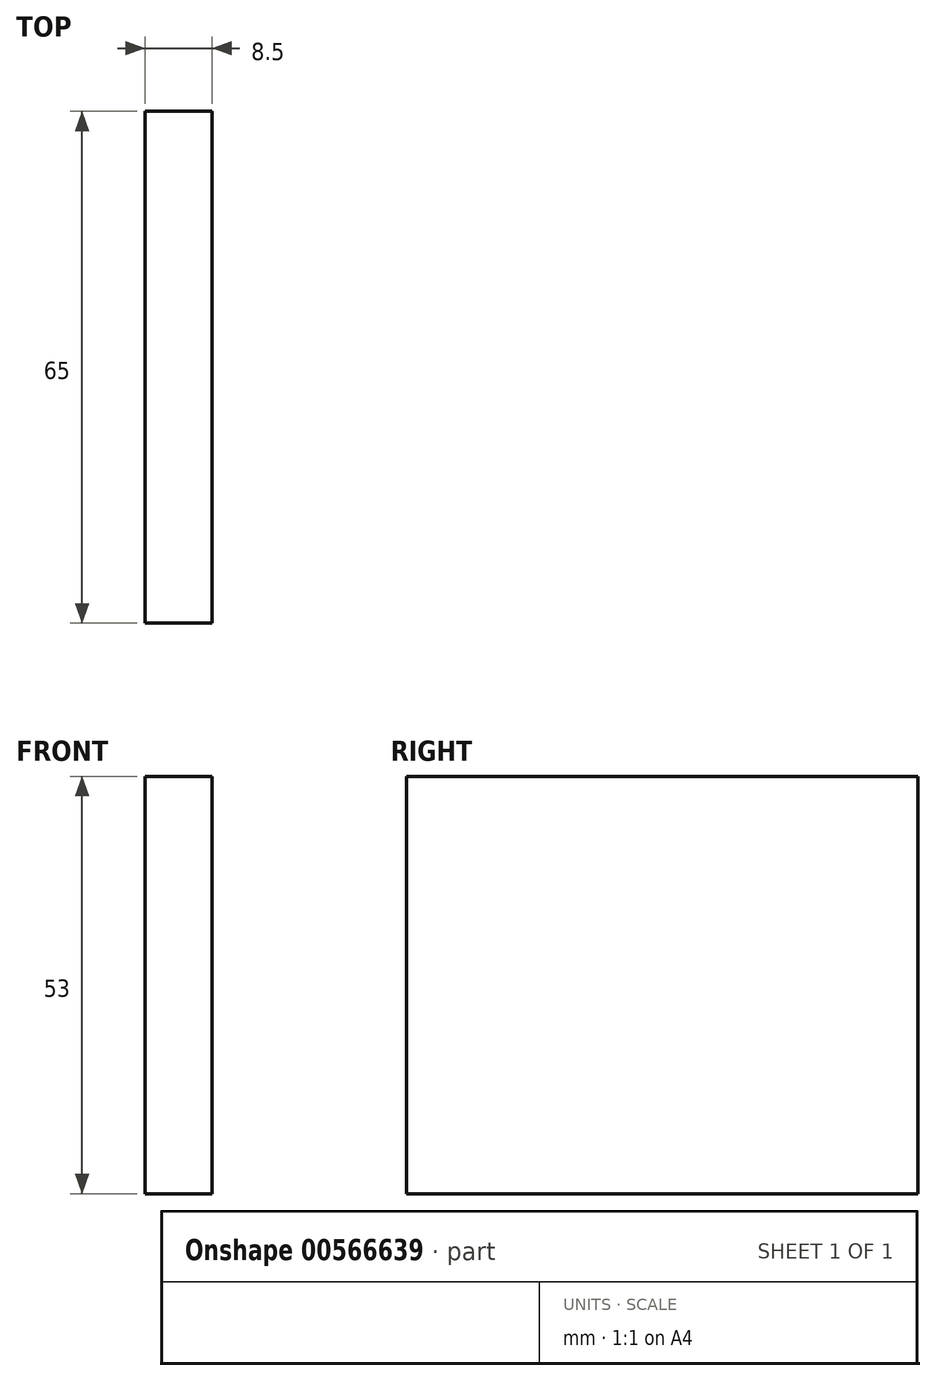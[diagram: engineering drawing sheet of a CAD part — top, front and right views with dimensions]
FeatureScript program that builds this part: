
annotation { "Feature Type Name" : "Feature", "Feature Type Description" : "" }
export const myFeature = defineFeature(function(context is Context, id is Id, definition is map)
    precondition{}
    {
        {
            var Q0;
            Q0=qCreatedBy(makeId("Right.planeOp"),FACE);
            var sketch = newSketch(context, id + "F0", { "sketchPlane" : qUnion([Q0])});
            skLineSegment(sketch, "E0.bottom", {"start": v(-32.5, 26.5) * mm, "end": v(32.5, 26.5) * mm});
            skLineSegment(sketch, "E0.top", {"start": v(-32.5, -26.5) * mm, "end": v(32.5, -26.5) * mm});
            skLineSegment(sketch, "E0.left", {"start": v(-32.5, 26.5) * mm, "end": v(-32.5, -26.5) * mm});
            skLineSegment(sketch, "E0.right", {"start": v(32.5, 26.5) * mm, "end": v(32.5, -26.5) * mm});
            skPoint(sketch, "E0.middle", {"position": v(0, 0) * mm});
            skSolve(sketch);
        }
        {
            var Q0;
            Q0=makeQuery(id+"F0.imprint","IMPRINT",FACE,{"disambiguationData":[TD([[makeQuery(id+"F0.imprint","IMPRINT",EDGE,{"derivedFrom":sQuery(id+"F0.wireOp",EDGE,"E0.bottom")}),-1.0]])]});
            extrude(context, id + "F1", {"entities" : qUnion([Q0]), "endBound" : BoundingType.SYMMETRIC, "depth" : 8.5 * mm, "offsetDistance" : 25 * mm});
        }
    });
